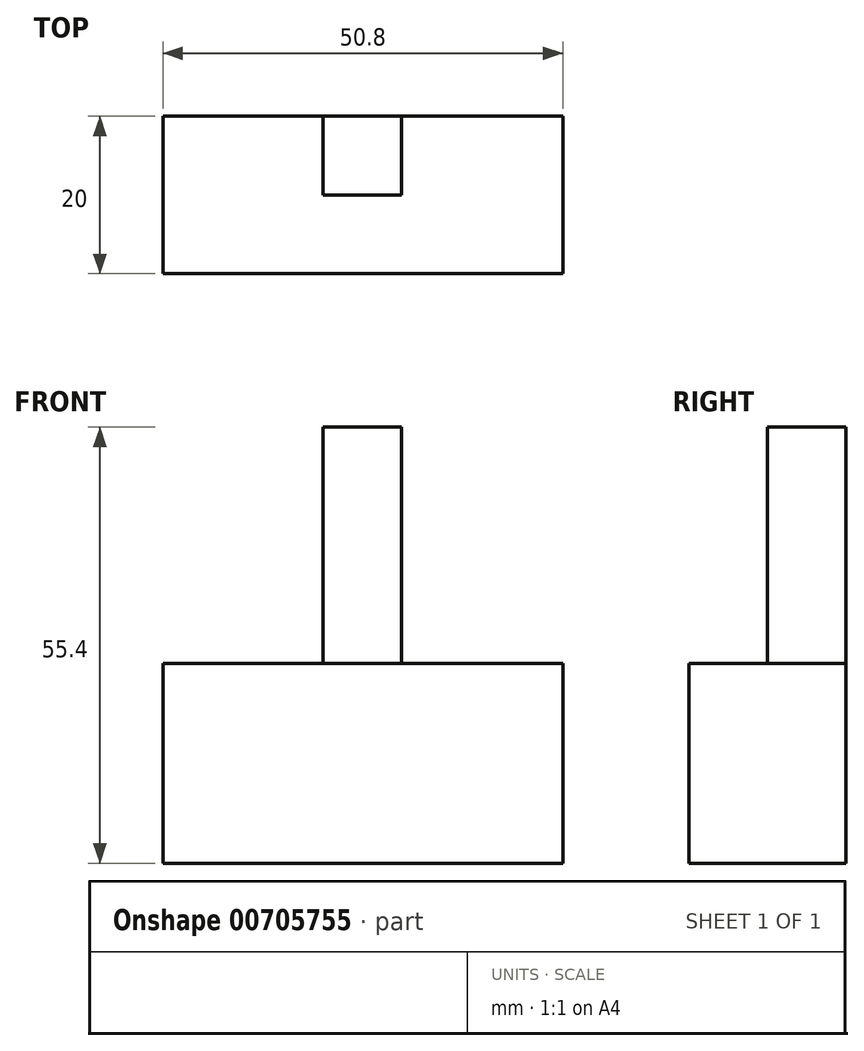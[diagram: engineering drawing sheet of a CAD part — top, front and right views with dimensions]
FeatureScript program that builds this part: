
annotation { "Feature Type Name" : "Feature", "Feature Type Description" : "" }
export const myFeature = defineFeature(function(context is Context, id is Id, definition is map)
    precondition{}
    {
        {
            var Q0;
            Q0=qCreatedBy(makeId("Front.planeOp"),FACE);
            var sketch = newSketch(context, id + "F0", { "sketchPlane" : qUnion([Q0])});
            skLineSegment(sketch, "E0.bottom", {"start": v(0, 0) * mm, "end": v(-50.8, 0) * mm});
            skLineSegment(sketch, "E0.top", {"start": v(0, 50.8) * mm, "end": v(-50.8, 50.8) * mm});
            skLineSegment(sketch, "E0.left", {"start": v(0, 0) * mm, "end": v(0, 50.8) * mm});
            skLineSegment(sketch, "E0.right", {"start": v(-50.8, 0) * mm, "end": v(-50.8, 50.8) * mm});
            skSolve(sketch);
        }
        {
            var Q0;
            Q0 = qSketchRegion(id + "F0", true);
            extrude(context, id + "F1", {"entities" : qUnion([Q0]), "depth" : 20 * mm, "offsetDistance" : 25.4 * mm});
        }
        {
            var Q0;
            Q0=makeQuery(id+"F1.opExtrude","SWEPT_FACE",FACE,{"disambiguationData":[OSD([sQuery(id+"F0.wireOp",EDGE,"E0.top")])]});
            var sketch = newSketch(context, id + "F2", { "sketchPlane" : qUnion([Q0])});
            skSolve(sketch);
        }
        {
            var Q0;
            Q0=makeQuery(id+"F1.opExtrude","SWEPT_FACE",FACE,{"disambiguationData":[OSD([sQuery(id+"F0.wireOp",EDGE,"E0.bottom")])]});
            extrude(context, id + "F3", {"entities" : qUnion([Q0]), "operationType" : NewBodyOperationType.REMOVE, "oppositeDirection" : true, "depth" : 25.4 * mm, "offsetDistance" : 25.4 * mm});
        }
        {
            var Q0;
            {var subQ0=sQuery(id+"F0.wireOp",EDGE,"E0.top");Q0=makeQuery(id+"F2.imprint","IMPRINT",FACE,{"disambiguationData":[TD([[makeQuery(id+"F2.imprint","IMPRINT",EDGE,{"derivedFrom":makeQuery(id+"F1.opExtrude","CAP_EDGE",EDGE,{"disambiguationData":[OSD([subQ0])],"isStart":true})}),1.0]])]});}
            var sketch = newSketch(context, id + "F4", { "sketchPlane" : qUnion([Q0])});
            skLineSegment(sketch, "E1.bottom", {"start": v(-20.47, 0) * mm, "end": v(-30.47, 0) * mm});
            skLineSegment(sketch, "E1.top", {"start": v(-20.47, -10) * mm, "end": v(-30.47, -10) * mm});
            skLineSegment(sketch, "E1.left", {"start": v(-20.47, 0) * mm, "end": v(-20.47, -10) * mm});
            skLineSegment(sketch, "E1.right", {"start": v(-30.47, 0) * mm, "end": v(-30.47, -10) * mm});
            skSolve(sketch);
        }
        {
            var Q0;
            Q0=makeQuery(id+"F4.imprint","IMPRINT",FACE,{"disambiguationData":[TD([[makeQuery(id+"F4.imprint","IMPRINT",EDGE,{"derivedFrom":sQuery(id+"F4.wireOp",EDGE,"E1.bottom")}),1.0]])]});
            extrude(context, id + "F5", {"entities" : qUnion([Q0]), "operationType" : NewBodyOperationType.ADD, "depth" : 30 * mm, "offsetDistance" : 25 * mm});
        }
    });
